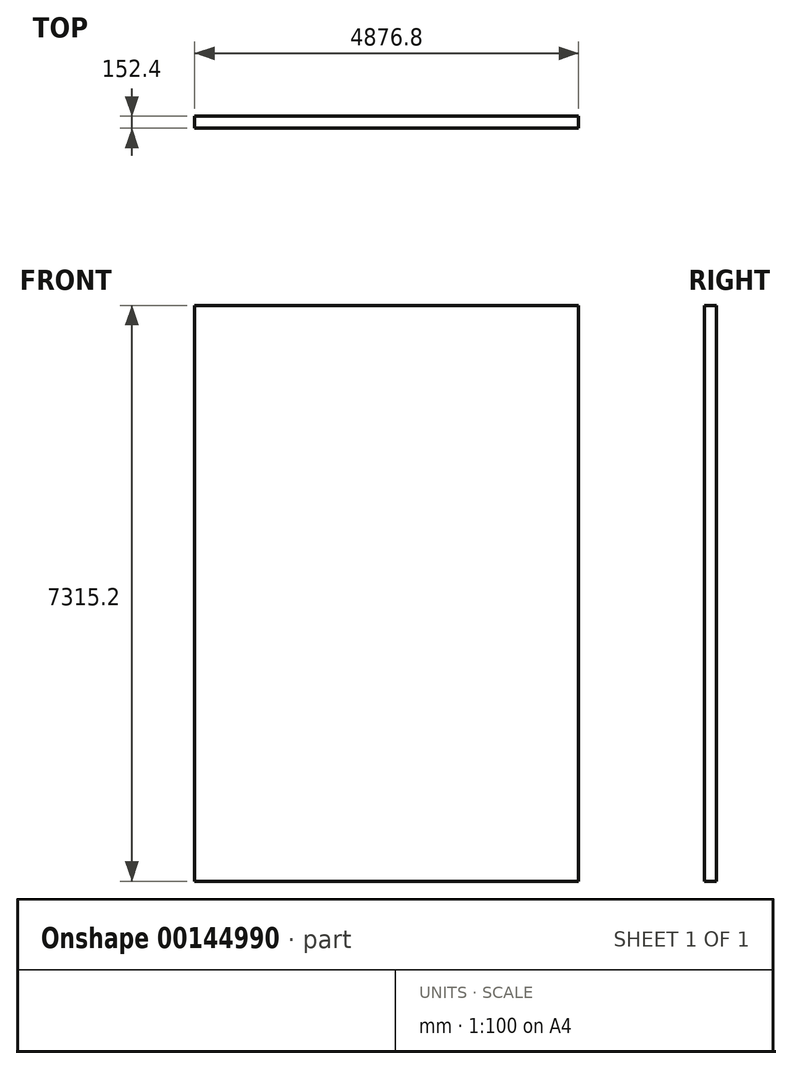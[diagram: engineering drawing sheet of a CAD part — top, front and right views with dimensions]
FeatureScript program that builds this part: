
annotation { "Feature Type Name" : "Feature", "Feature Type Description" : "" }
export const myFeature = defineFeature(function(context is Context, id is Id, definition is map)
    precondition{}
    {
        {
            var Q0;
            Q0=qCreatedBy(makeId("Front.planeOp"),FACE);
            var sketch = newSketch(context, id + "F0", { "sketchPlane" : qUnion([Q0])});
            skLineSegment(sketch, "E0.bottom", {"start": v(0, 0) * mm, "end": v(4876.8, 0) * mm});
            skLineSegment(sketch, "E0.top", {"start": v(0, 7315.2) * mm, "end": v(4876.8, 7315.2) * mm});
            skLineSegment(sketch, "E0.left", {"start": v(0, 0) * mm, "end": v(0, 7315.2) * mm});
            skLineSegment(sketch, "E0.right", {"start": v(4876.8, 0) * mm, "end": v(4876.8, 7315.2) * mm});
            skSolve(sketch);
        }
        {
            var Q0;
            Q0 = qSketchRegion(id + "F0", true);
            extrude(context, id + "F1", {"entities" : qUnion([Q0]), "depth" : 152.4 * mm});
        }
    });
